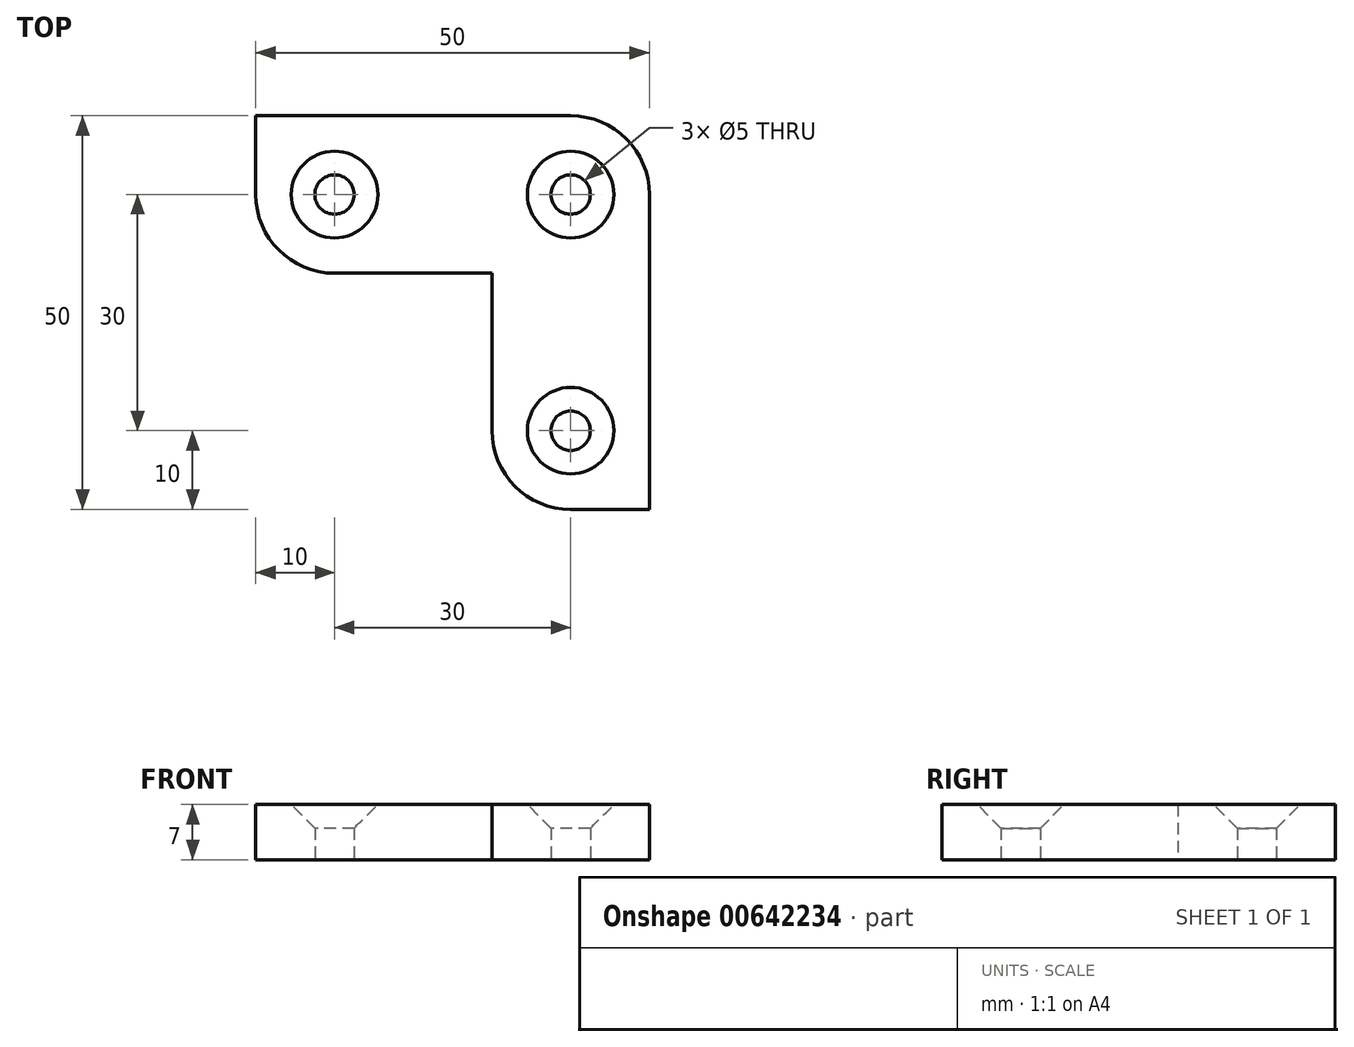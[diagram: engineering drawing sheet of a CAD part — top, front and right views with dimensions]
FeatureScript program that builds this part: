
annotation { "Feature Type Name" : "Feature", "Feature Type Description" : "" }
export const myFeature = defineFeature(function(context is Context, id is Id, definition is map)
    precondition{}
    {
        {
            var Q0;
            Q0=qCreatedBy(makeId("Top.planeOp"),FACE);
            var sketch = newSketch(context, id + "F0", { "sketchPlane" : qUnion([Q0])});
            skLineSegment(sketch, "E0", {"start": v(0, 0) * mm, "end": v(-50, 0) * mm});
            skLineSegment(sketch, "E1", {"start": v(-50, 0) * mm, "end": v(-50, -20) * mm});
            skLineSegment(sketch, "E2", {"start": v(-50, -20) * mm, "end": v(-20, -20) * mm});
            skLineSegment(sketch, "E3", {"start": v(-20, -20) * mm, "end": v(-20, -50) * mm});
            skLineSegment(sketch, "E4", {"start": v(-20, -50) * mm, "end": v(0, -50) * mm});
            skLineSegment(sketch, "E5", {"start": v(0, -50) * mm, "end": v(0, 0) * mm});
            skCircle(sketch, "E6", {"center": v(-40, -10) * mm, "radius": 2.5 * mm});
            skCircle(sketch, "E7", {"center": v(-10, -40) * mm, "radius": 2.5 * mm});
            skCircle(sketch, "E8", {"center": v(-10, -10) * mm, "radius": 2.5 * mm});
            skSolve(sketch);
        }
        {
            var Q0;
            Q0=makeQuery(id+"F0.imprint","IMPRINT",FACE,{"disambiguationData":[TD([[makeQuery(id+"F0.imprint","IMPRINT",EDGE,{"derivedFrom":sQuery(id+"F0.wireOp",EDGE,"E0")}),1.0]])]});
            extrude(context, id + "F1", {"entities" : qUnion([Q0]), "depth" : 7 * mm, "offsetDistance" : 25 * mm});
        }
        {
            var Q0;
            Q0=makeQuery(id+"F1.opExtrude","SWEPT_EDGE",EDGE,{"disambiguationData":[OSD([sQuery(id+"F0.wireOp",EDGE,"E0"),sQuery(id+"F0.wireOp",EDGE,"E5")])]});
            var Q1;
            Q1=makeQuery(id+"F1.opExtrude","SWEPT_EDGE",EDGE,{"disambiguationData":[OSD([sQuery(id+"F0.wireOp",EDGE,"E3"),sQuery(id+"F0.wireOp",EDGE,"E4")])]});
            var Q2;
            Q2=makeQuery(id+"F1.opExtrude","SWEPT_EDGE",EDGE,{"disambiguationData":[OSD([sQuery(id+"F0.wireOp",EDGE,"E1"),sQuery(id+"F0.wireOp",EDGE,"E2")])]});
            fillet(context, id + "F2", {"entities" : qUnion([Q0, Q1, Q2]), "radius" : 10 * mm, "tangentPropagation" : true, "allowEdgeOverflow" : false});
        }
        {
            var Q0;
            Q0=makeQuery(id+"F1.opExtrude","CAP_EDGE",EDGE,{"disambiguationData":[OSD([sQuery(id+"F0.wireOp",EDGE,"E6")])],"isStart":false});
            var Q1;
            Q1=makeQuery(id+"F1.opExtrude","CAP_EDGE",EDGE,{"disambiguationData":[OSD([sQuery(id+"F0.wireOp",EDGE,"kFnQQ2b6-yyFc-0bB7-Qnwg-1zTSAdxvF5WS")])],"isStart":false});
            var Q2;
            Q2=makeQuery(id+"F1.opExtrude","CAP_EDGE",EDGE,{"disambiguationData":[OSD([sQuery(id+"F0.wireOp",EDGE,"ch5n2Qrf-17dX-lXG1-GB67-5zehkUahqHRW")])],"isStart":false});
            var Q3;
            Q3=makeQuery(id+"F1.opExtrude","CAP_EDGE",EDGE,{"disambiguationData":[OSD([sQuery(id+"F0.wireOp",EDGE,"E7")])],"isStart":false});
            var Q4;
            Q4=makeQuery(id+"F1.opExtrude","CAP_EDGE",EDGE,{"disambiguationData":[OSD([sQuery(id+"F0.wireOp",EDGE,"E8")])],"isStart":false});
            chamfer(context, id + "F3", {"entities" : qUnion([Q0, Q1, Q2, Q3, Q4]), "width" : 3 * mm, "tangentPropagation" : true});
        }
    });
